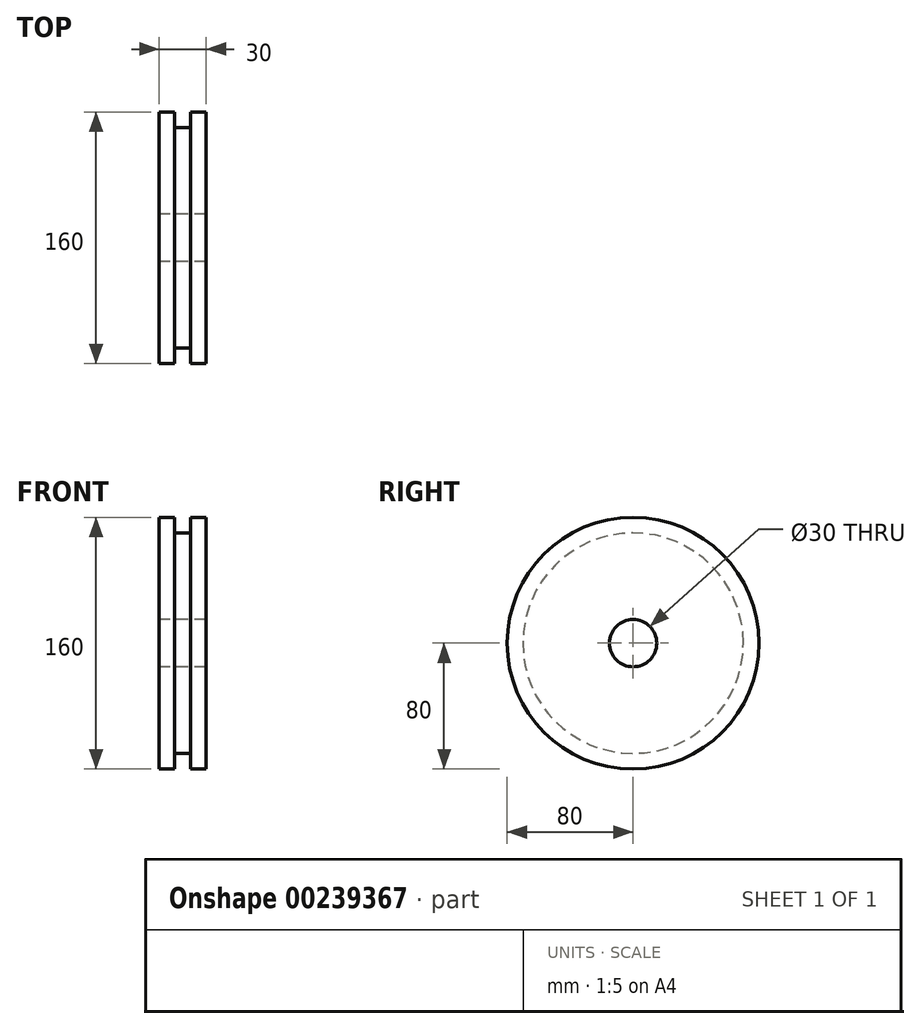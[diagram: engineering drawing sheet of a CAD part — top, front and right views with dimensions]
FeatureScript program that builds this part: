
annotation { "Feature Type Name" : "Feature", "Feature Type Description" : "" }
export const myFeature = defineFeature(function(context is Context, id is Id, definition is map)
    precondition{}
    {
        {
            var Q0;
            Q0=qCreatedBy(makeId("Front.planeOp"),FACE);
            var sketch = newSketch(context, id + "F0", { "sketchPlane" : qUnion([Q0])});
            skLineSegment(sketch, "E0", {"start": v(0, 15) * mm, "end": v(0, 80) * mm});
            skLineSegment(sketch, "E1", {"start": v(0, 80) * mm, "end": v(10, 80) * mm});
            skLineSegment(sketch, "E2", {"start": v(10, 80) * mm, "end": v(10, 70) * mm});
            skLineSegment(sketch, "E3", {"start": v(10, 70) * mm, "end": v(20, 70) * mm});
            skLineSegment(sketch, "E4", {"start": v(20, 70) * mm, "end": v(20, 80) * mm});
            skLineSegment(sketch, "E5", {"start": v(20, 80) * mm, "end": v(30, 80) * mm});
            skLineSegment(sketch, "E6", {"start": v(30, 80) * mm, "end": v(30, 15) * mm});
            skLineSegment(sketch, "E7", {"start": v(0, 15) * mm, "end": v(30, 15) * mm});
            skLineSegment(sketch, "E8", {"start": v(0, 0) * mm, "end": v(79.76, 0) * mm, "construction": true});
            skSolve(sketch);
        }
        {
            var Q0;
            Q0=makeQuery(id+"F0.imprint","IMPRINT",FACE,{"disambiguationData":[TD([[makeQuery(id+"F0.imprint","IMPRINT",EDGE,{"derivedFrom":sQuery(id+"F0.wireOp",EDGE,"E0")}),-1.0]])]});
            var Q1;
            Q1=sQuery(id+"F0.wireOp",EDGE,"E8");
            revolve(context, id + "F1", {"entities" : qUnion([Q0]), "axis" : qUnion([Q1]), "revolveType" : RevolveType.FULL});
        }
    });
